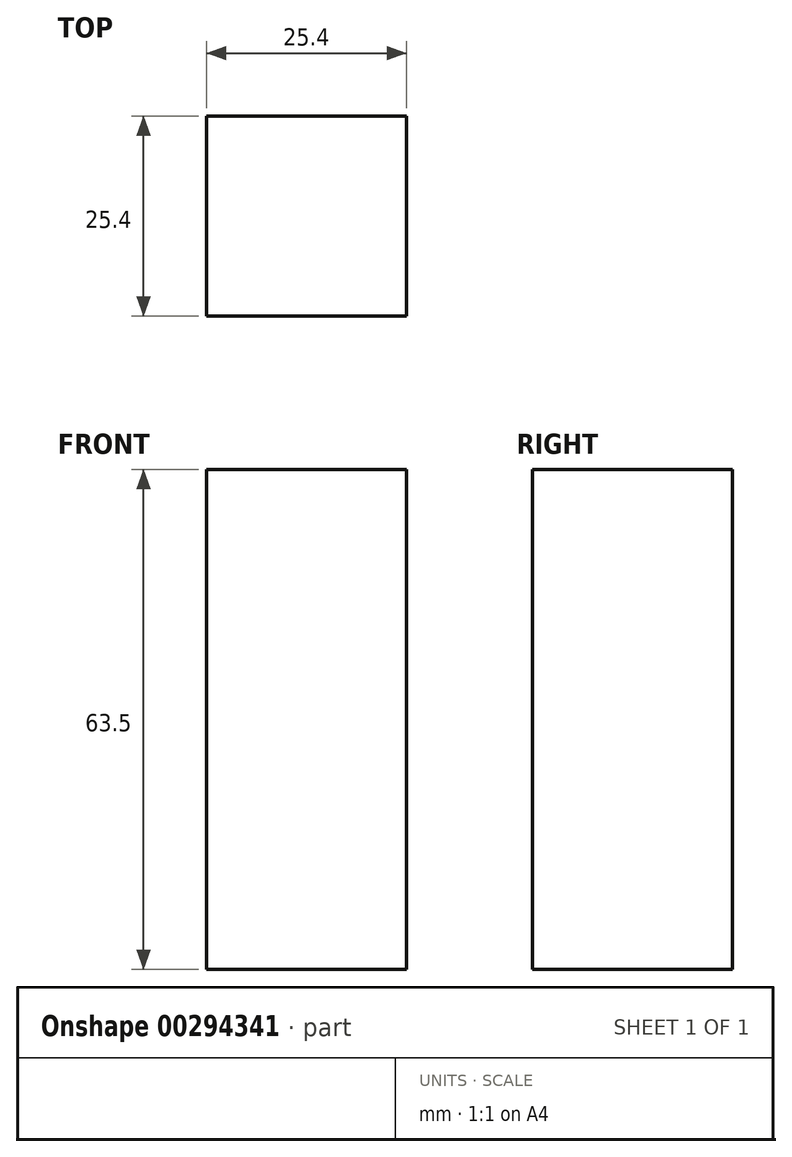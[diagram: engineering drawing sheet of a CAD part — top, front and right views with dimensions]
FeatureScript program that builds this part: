
annotation { "Feature Type Name" : "Feature", "Feature Type Description" : "" }
export const myFeature = defineFeature(function(context is Context, id is Id, definition is map)
    precondition{}
    {
        {
            var Q0;
            Q0=qCreatedBy(makeId("Front.planeOp"),FACE);
            var sketch = newSketch(context, id + "F0", { "sketchPlane" : qUnion([Q0])});
            skLineSegment(sketch, "E0.bottom", {"start": v(-13.05, 34.61) * mm, "end": v(12.35, 34.61) * mm});
            skLineSegment(sketch, "E0.top", {"start": v(-13.05, -28.89) * mm, "end": v(12.35, -28.89) * mm});
            skLineSegment(sketch, "E0.left", {"start": v(-13.05, 34.61) * mm, "end": v(-13.05, -28.89) * mm});
            skLineSegment(sketch, "E0.right", {"start": v(12.35, 34.61) * mm, "end": v(12.35, -28.89) * mm});
            skSolve(sketch);
        }
        {
            var Q0;
            Q0 = qSketchRegion(id + "F0", true);
            extrude(context, id + "F1", {"entities" : qUnion([Q0]), "depth" : 25.4 * mm});
        }
    });
